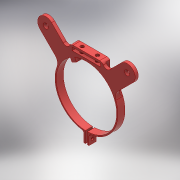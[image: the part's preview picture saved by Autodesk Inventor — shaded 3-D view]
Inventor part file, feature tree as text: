
AUTODESK INVENTOR PART (.ipt)
format: ipt  version: 2018 (Build 220112000, 112)  size: 336,384 bytes
history: native  units: mm
features: extrude x7, sketch x6, fillet x2, plane x2, projected_geometry x2
ambient origin geometry x8: Origin, YZ Plane, XZ Plane, XY Plane, X Axis, Y Axis, Z Axis, Center Point
bodies: Solid1 (feature_tree)
feature tree (19):
  extrude  "Extrusion1"  Depth=80.0mm
  extrude  "Extrusion2"  Depth=5.0mm
  extrude  "Extrusion4"  Depth=68.282mm
  extrude  "Extrusion5"  TaperAngle=45.0deg  [1 undecoded]
  extrude  "Extrusion6"  Depth=8.0mm
  fillet  "Fillet1"  Radius=1.0mm
  fillet  "Fillet2"  Radius=1.5mm
  extrude  "Extrusion7"  Depth=10.0mm
  plane  "Work Plane1"
  extrude  "Extrusion3"  Depth=10.0mm TaperAngle=0.0deg
  sketch  "Sketch2"  dims[d0=80.0mm d1=80.0mm]
  projected_geometry  "Projected Loop1"
  sketch  "Sketch3"  dims[d2=5.0mm d3=5.0mm]
  plane  "Work Plane2"
  sketch  "Sketch4"  dims[d5=59.5mm d6=68.282mm]
  sketch  "Sketch5"  dims[d8=8.0mm d9=45.0deg]
  sketch  "Sketch7"  dims[d10=1.2mm d11=8.0mm d12=1.0mm d13=1.5mm]
  projected_geometry  "Projected Loop2"
  sketch  "Sketch8"  dims[d14=10.0mm d15=2.0mm d16=3.0mm d17=0.0mm d18=1.2mm d19=8.0mm d20=4.0mm d21=0.0mm d22=4.0mm d24=4.0mm d25=0.0mm d26=3.0mm d27=24.0mm d28=5.0mm d29=26.0mm d30=4.782202mm d31=4.0mm d32=0.0mm d33=3.0mm d34=4.0mm d35=4.0mm d36=0.0mm d37=3.0mm d38=28.0mm d39=1.0mm d43=2.0mm d45=2.0mm d46=2.0mm d47=4.0mm d48=0.0mm d49=4.0mm d50=3.5mm d51=3.5mm d52=15.0mm d53=4.0mm d54=0.0mm]
note: 1 required parameter value undecoded (feature->parameter linkage not recoverable at this tier; creation-order binding heuristic only, values carry confidence <= 0.55)
